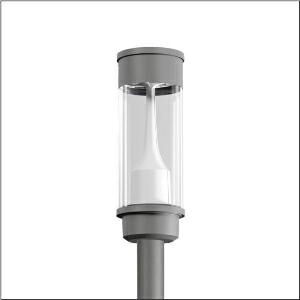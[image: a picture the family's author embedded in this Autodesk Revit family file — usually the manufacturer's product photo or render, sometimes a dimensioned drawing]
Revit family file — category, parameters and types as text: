
# Revit family: litepole_iq___p1_0a_5xa5415lf14h_d8b4
name_source: partatom
category: Lighting Fixtures
units: mm (PartAtom-declared; Revit-internal decimal feet)

## family parameters
Cut with Voids When Loaded = No
Host = Face
Light Source = No
Part Type = Normal
Room Calculation Point = No
Round Connector Dimension = Use Diameter
Shared = No

## types (1)
- --- (1 x LED, 1510 lm, 10 W, 4000K)
    Apparent Load = 10 VA
    CIE Flux Codes = 32 61 90 93 100
    Color Rendering = 70
    Color Temperature = 4000K
    Default Elevation = 1800 mm
    Description = Litepole iQ, mast luminaire, Module 540 iQ-SR, primary light control with 3 zone facetted reflector, of plastic, silver coated, highly specular, structured, primary optical cover: cover, of PMMA, transparent, partly coated, light distribution: P1.0a, light emission: direct distribution, primary light characteristic: strongly asymmetric, installation type: post-top, LED, High Power LED, rated luminous flux: 1.510lm, luminous efficacy: 151lm/W, light colour: 740, colour temperature: 4000K, control gear: ECG iQ, control: optimised constant luminous flux control (CLO 2.0), Desk-Remote (wireless, voltage-free reading and setting of iQ features in the workshop via application-optimized NFC function/RFID function), Light-Fading, Smart-Wire, Night-Set, Lumen-Switch, Temp-Guard, Auto-Match, Street-Remote, pre-setting: logarithmic dimming characteristic, with terminal, 6-pole, max. 2.5mm², mains connection: 230..240V, AC, 50/60Hz, start of lifetime: 10W, end of service life: 10W, reduction: 5W, luminaire housing, upper part, of glass-fibre reinforced polyester, coated, Siteco® metallic grey (DB 702S), diameter: 210mm, height: 590mm, spigot size: d x l = 76 x 70mm (post-top) | with reducer (optional accessory) 60 x 70mm, post-top mast mounting element, of diecast aluminium, coated, Siteco® metallic grey (DB 702S), Module 540 iQ-SR, traffic white (RAL 9016), equipment: standard, protection rating (complete): IP65, insulation class (complete): insulation class II (safety insulation), certification: CE, ENEC, VDE, packaging unit: 1 piece

Light Distribution: P1.0a
    Height = 590 mm
    Lamp = 1 x LED
    Lamp Light Flux = 1510 lm
    Lamp Power = 10 W
    Lamp count = 1
    Length = 220 mm
    Luminous efficacy = 151 lm/W
    Manufacturer = Siteco
    ModVariant = No
    Model = 5XA5415LF14H
    Number of Poles = 1
    OnlyDefault = Yes
    Power Factor = 1
    Product Name = Litepole iQ | P1.0a
    Product group = mast luminaire | pylon top
    ProductGroupID = 6100
    Protection Class = Protection class II
    Protection Degree = IP 65
    RLX_Detail_Level = 1
    RLX_Emergency_Light_Flux = 0 lm
    RLX_Emergency_Type = 0
    RLX_Emergency_Type_DB = No
    RlxData = <blob elided: 68321 chars, md5=26dceac8>
    Socket = socket
    Standby Power = 0 W
    System Light Flux = 1510 lm
    System Power = 10 W
    Type Comments = factory setting: luminous flux: 100 % | dim-lin: 254 | 401 mA
    Type Image = l_1006025.jpg
    URL = http://relux.com
    VarID = @adj_129055
    Voltage = 0 V
    Weight = 0.00 kg
    Width = 0 mm  [stored 0 ft]

note: [stored X ft] marks values corroborated as IEEE doubles in the binary element streams (Revit-internal decimal feet)

## geometry (parser evidence)
native form markers: Blend x4, Sweep x13
no freeform markers — native parametric forms only
